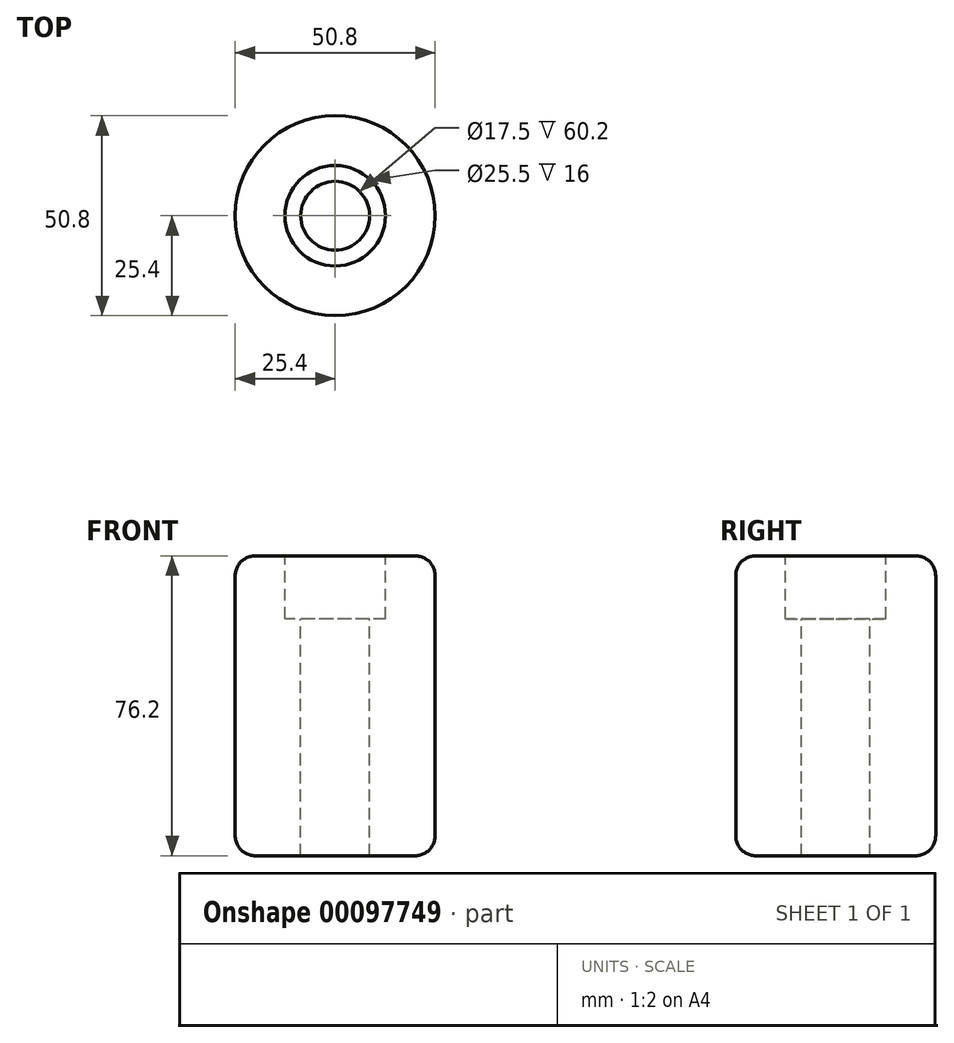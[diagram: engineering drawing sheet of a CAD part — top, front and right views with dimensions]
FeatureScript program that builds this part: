
annotation { "Feature Type Name" : "Feature", "Feature Type Description" : "" }
export const myFeature = defineFeature(function(context is Context, id is Id, definition is map)
    precondition{}
    {
        {
            var Q0;
            Q0=qCreatedBy(makeId("Top.planeOp"),FACE);
            var sketch = newSketch(context, id + "F0", { "sketchPlane" : qUnion([Q0])});
            skCircle(sketch, "E0", {"center": v(0, 0) * mm, "radius": 25.4 * mm});
            skSolve(sketch);
        }
        {
            var Q0;
            Q0 = qSketchRegion(id + "F0", true);
            extrude(context, id + "F1", {"entities" : qUnion([Q0]), "depth" : 76.2 * mm});
        }
        {
            var Q0;
            Q0=makeQuery(id+"F1.opExtrude","CAP_FACE",FACE,{"disambiguationData":[OSD([sQuery(id+"F0.wireOp",EDGE,"E0")])],"isStart":false});
            var sketch = newSketch(context, id + "F2", { "sketchPlane" : qUnion([Q0])});
            skPoint(sketch, "E1", {"position": v(0, 0) * mm});
            skSolve(sketch);
        }
        {
            var Q0;
            Q0=sQuery(id+"F2.wireOp",VERTEX,"E1");
            var Q1;
            Q1=makeQuery(id+"F1.opExtrude","SWEPT_BODY",BODY,{"disambiguationData":[OSD([sQuery(id+"F0.wireOp",EDGE,"E0")])]});
            hole(context, id + "F3", {"style" : HoleStyle.C_BORE, "endStyle" : HoleEndStyle.THROUGH, "standardTappedOrClearance" : lookupTablePath({ "standard" : "ISO", "fit" : "Normal", "size" : "M16", "type" : "Clearance" }), "standardBlindInLast" : lookupTablePath({ "fit" : "Standard", "standard" : "ISO", "size" : "M16", "type" : "Clearance" }), "holeDiameter" : 17.5 * mm, "cBoreDiameter" : 25.5 * mm, "cBoreDepth" : 16 * mm, "locations" : qUnion([Q0]), "scope" : qUnion([Q1]), "isTappedThrough" : true});
        }
        {
            var Q0;
            Q0=makeQuery(id+"F1.opExtrude","CAP_EDGE",EDGE,{"disambiguationData":[OSD([sQuery(id+"F0.wireOp",EDGE,"E0")])],"isStart":false});
            var Q1;
            Q1=makeQuery(id+"F1.opExtrude","CAP_EDGE",EDGE,{"disambiguationData":[OSD([sQuery(id+"F0.wireOp",EDGE,"E0")])],"isStart":true});
            fillet(context, id + "F4", {"entities" : qUnion([Q0, Q1]), "radius" : 5.08 * mm, "tangentPropagation" : true, "allowEdgeOverflow" : false});
        }
    });
